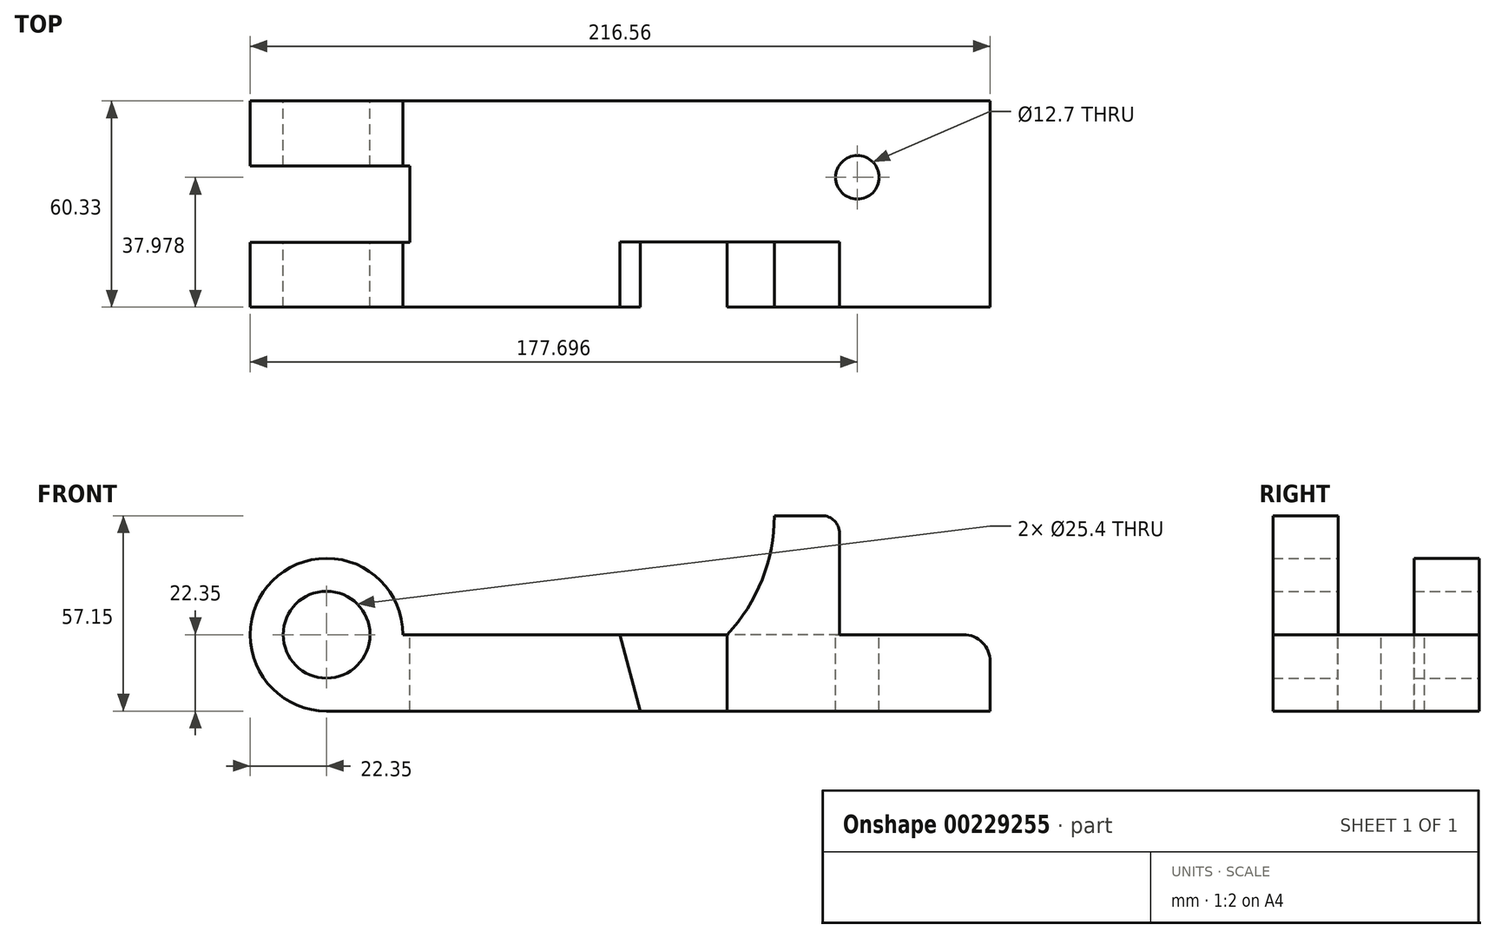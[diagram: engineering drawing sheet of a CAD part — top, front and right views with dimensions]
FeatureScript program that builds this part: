
annotation { "Feature Type Name" : "Feature", "Feature Type Description" : "" }
export const myFeature = defineFeature(function(context is Context, id is Id, definition is map)
    precondition{}
    {
        {
            var Q0;
            Q0=qCreatedBy(makeId("Front.planeOp"),FACE);
            var sketch = newSketch(context, id + "F0", { "sketchPlane" : qUnion([Q0])});
            skLineSegment(sketch, "E0", {"start": v(0, 0) * mm, "end": v(22.35, 0) * mm});
            skArc(sketch, "E1", {"start": v(22.35, 0) * mm, "mid": v(-15.8, 15.8) * mm, "end": v(0, -22.35) * mm});
            skCircle(sketch, "E2", {"center": v(0, 0) * mm, "radius": 12.7 * mm});
            skLineSegment(sketch, "E3", {"start": v(0, -22.35) * mm, "end": v(194.2, -22.35) * mm});
            skLineSegment(sketch, "E4", {"start": v(0, 0) * mm, "end": v(117.25, 0) * mm});
            skLineSegment(sketch, "E5", {"start": v(194.2, -22.35) * mm, "end": v(194.2, -7.87) * mm});
            skArc(sketch, "E6.filletArc", {"start": v(194.2, -7.87) * mm, "mid": v(191.9, -2.3) * mm, "end": v(186.33, 0) * mm});
            skLineSegment(sketch, "E7", {"start": v(150.09, 0) * mm, "end": v(150.09, 29.72) * mm});
            skLineSegment(sketch, "E8", {"start": v(145, 34.8) * mm, "end": v(131.04, 34.8) * mm});
            skLineSegment(sketch, "E9.trimOffspring", {"start": v(150.09, 0) * mm, "end": v(186.33, 0) * mm});
            skPoint(sketch, "E10.visualSharp", {"position": v(150.09, 34.8) * mm});
            skArc(sketch, "E10.filletArc", {"start": v(150.09, 29.72) * mm, "mid": v(148.6, 33.31) * mm, "end": v(145, 34.8) * mm});
            skPoint(sketch, "E11.start.orphan", {"position": v(0, -40.15) * mm});
            skPoint(sketch, "E12.orphan", {"position": v(117.25, -40.15) * mm});
            skArc(sketch, "E13", {"start": v(117.25, 0) * mm, "mid": v(127.46, 16.08) * mm, "end": v(131.04, 34.8) * mm});
            skSolve(sketch);
        }
        {
            var Q0;
            Q0 = qSketchRegion(id + "F0", true);
            extrude(context, id + "F1", {"entities" : qUnion([Q0]), "depth" : 60.32 * mm});
        }
        {
            var Q0;
            Q0=makeQuery(id+"F1.opExtrude","CAP_FACE",FACE,{"disambiguationData":[OSD([sQuery(id+"F0.wireOp",EDGE,"E1"),sQuery(id+"F0.wireOp",EDGE,"E2"),sQuery(id+"F0.wireOp",EDGE,"E3"),sQuery(id+"F0.wireOp",EDGE,"E4"),sQuery(id+"F0.wireOp",EDGE,"E5"),sQuery(id+"F0.wireOp",EDGE,"E6.filletArc"),sQuery(id+"F0.wireOp",EDGE,"E7"),sQuery(id+"F0.wireOp",EDGE,"E8"),sQuery(id+"F0.wireOp",EDGE,"E9.trimOffspring"),sQuery(id+"F0.wireOp",EDGE,"E10.filletArc"),sQuery(id+"F0.wireOp",EDGE,"E13")])],"isStart":false});
            var sketch = newSketch(context, id + "F2", { "sketchPlane" : qUnion([Q0])});
            skLineSegment(sketch, "E14", {"start": v(117.25, -22.35) * mm, "end": v(117.25, 0) * mm});
            skLineSegment(sketch, "E15", {"start": v(91.85, -22.35) * mm, "end": v(85.85, 0) * mm});
            skLineSegment(sketch, "E16", {"start": v(85.85, 0) * mm, "end": v(117.25, 0) * mm});
            skLineSegment(sketch, "E17", {"start": v(91.85, -22.35) * mm, "end": v(117.25, -22.35) * mm});
            skSolve(sketch);
        }
        {
            var Q0;
            Q0 = qSketchRegion(id + "F2", true);
            extrude(context, id + "F3", {"entities" : qUnion([Q0]), "operationType" : NewBodyOperationType.REMOVE, "oppositeDirection" : true, "depth" : 19.05 * mm});
        }
        {
            var Q0;
            Q0=qCreatedBy(makeId("Top.planeOp"),FACE);
            var sketch = newSketch(context, id + "F4", { "sketchPlane" : qUnion([Q0])});
            skLineSegment(sketch, "E18", {"start": v(-22.35, -19) * mm, "end": v(24.34, -19) * mm});
            skLineSegment(sketch, "E19", {"start": v(24.34, -19) * mm, "end": v(24.34, -41.33) * mm});
            skLineSegment(sketch, "E20", {"start": v(24.34, -41.33) * mm, "end": v(-22.35, -41.33) * mm});
            skPoint(sketch, "E21.orphan", {"position": v(0, 0) * mm});
            skLineSegment(sketch, "E22", {"start": v(-22.35, -19) * mm, "end": v(-22.35, -41.33) * mm});
            skPoint(sketch, "E23.orphan", {"position": v(24.34, -60.33) * mm});
            skSolve(sketch);
        }
        {
            var Q0;
            Q0 = qSketchRegion(id + "F4", true);
            extrude(context, id + "F5", {"entities" : qUnion([Q0]), "operationType" : NewBodyOperationType.REMOVE, "endBound" : BoundingType.SYMMETRIC, "oppositeDirection" : true, "depth" : 254 * mm});
        }
        {
            var Q0;
            Q0=qCreatedBy(makeId("Top.planeOp"),FACE);
            var sketch = newSketch(context, id + "F6", { "sketchPlane" : qUnion([Q0])});
            skLineSegment(sketch, "E24", {"start": v(194.2, 0) * mm, "end": v(194.2, -22.35) * mm});
            skLineSegment(sketch, "E25", {"start": v(194.2, 0) * mm, "end": v(155.35, 0) * mm});
            skLineSegment(sketch, "E26", {"start": v(155.35, 0) * mm, "end": v(155.35, -22.35) * mm});
            skCircle(sketch, "E27", {"center": v(155.35, -22.35) * mm, "radius": 6.35 * mm});
            skSolve(sketch);
        }
        {
            var Q0;
            Q0 = qSketchRegion(id + "F6", true);
            extrude(context, id + "F7", {"entities" : qUnion([Q0]), "operationType" : NewBodyOperationType.REMOVE, "oppositeDirection" : true, "depth" : 254 * mm});
        }
        {
            var Q0;
            Q0=makeQuery(id+"F1.opExtrude","CAP_FACE",FACE,{"disambiguationData":[OSD([sQuery(id+"F0.wireOp",EDGE,"E1"),sQuery(id+"F0.wireOp",EDGE,"E2"),sQuery(id+"F0.wireOp",EDGE,"E3"),sQuery(id+"F0.wireOp",EDGE,"E4"),sQuery(id+"F0.wireOp",EDGE,"E5"),sQuery(id+"F0.wireOp",EDGE,"E6.filletArc"),sQuery(id+"F0.wireOp",EDGE,"E7"),sQuery(id+"F0.wireOp",EDGE,"E8"),sQuery(id+"F0.wireOp",EDGE,"E9.trimOffspring"),sQuery(id+"F0.wireOp",EDGE,"E10.filletArc"),sQuery(id+"F0.wireOp",EDGE,"E13")])],"isStart":true});
            var sketch = newSketch(context, id + "F8", { "sketchPlane" : qUnion([Q0])});
            skLineSegment(sketch, "E28", {"start": v(-150.09, 0) * mm, "end": v(-150.09, 29.72) * mm});
            skLineSegment(sketch, "E29", {"start": v(-145, 34.8) * mm, "end": v(-131.04, 34.8) * mm});
            skArc(sketch, "E30", {"start": v(-131.04, 34.8) * mm, "mid": v(-127.46, 16.08) * mm, "end": v(-117.25, 0) * mm});
            skPoint(sketch, "E31.visualSharp", {"position": v(-150.09, 34.8) * mm});
            skArc(sketch, "E31.filletArc", {"start": v(-145, 34.8) * mm, "mid": v(-148.6, 33.31) * mm, "end": v(-150.09, 29.72) * mm});
            skLineSegment(sketch, "E32", {"start": v(-150.09, 0) * mm, "end": v(-117.25, 0) * mm});
            skSolve(sketch);
        }
        {
            var Q0;
            Q0 = qSketchRegion(id + "F8", true);
            extrude(context, id + "F9", {"entities" : qUnion([Q0]), "operationType" : NewBodyOperationType.REMOVE, "oppositeDirection" : true, "depth" : 41.27 * mm});
        }
    });
